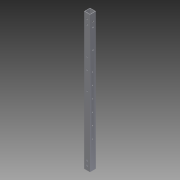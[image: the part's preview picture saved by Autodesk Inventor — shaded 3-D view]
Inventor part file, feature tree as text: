
AUTODESK INVENTOR PART (.ipt)
format: ipt  version: 2014 SP1 (Build 180222100, 222)  size: 130,560 bytes
history: native  units: in
note: dims shown in document units (in); Inventor stores cm internally (conversion verified against a paired STEP export)
features: reference x13, extrude x3, sketch x3
ambient origin geometry x8: Origin, YZ Plane, XZ Plane, XY Plane, X Axis, Y Axis, Z Axis, Center Point
bodies: Solid1 (feature_tree)
feature tree (19):
  extrude  "Extrusion1"  Depth=1.0in
  extrude  "Extrusion7"  Depth=23.5in TaperAngle=0.0deg
  extrude  "Extrusion8"  Depth=1.0in TaperAngle=0.0deg
  sketch  "Sketch1"  dims[d0=1.0in d2=1.0in]
  sketch  "Sketch8"  dims[d3=0.0625in d4=23.5in d5=0.0in]
  sketch  "Sketch9"  dims[d20=1.0in d21=0.0in d22=1.0in d23=0.0in d24=1.25in d25=0.875in d26=0.266in]
  reference  "Reference15"
  reference  "Reference16"
  reference  "Reference18"
  reference  "Reference21"
  reference  "Reference22"
  reference  "Reference23"
  reference  "Reference24"
  reference  "Reference25"
  reference  "Reference26"
  reference  "Reference27"
  reference  "Reference28"
  reference  "Reference29"
  reference  "Reference33"
